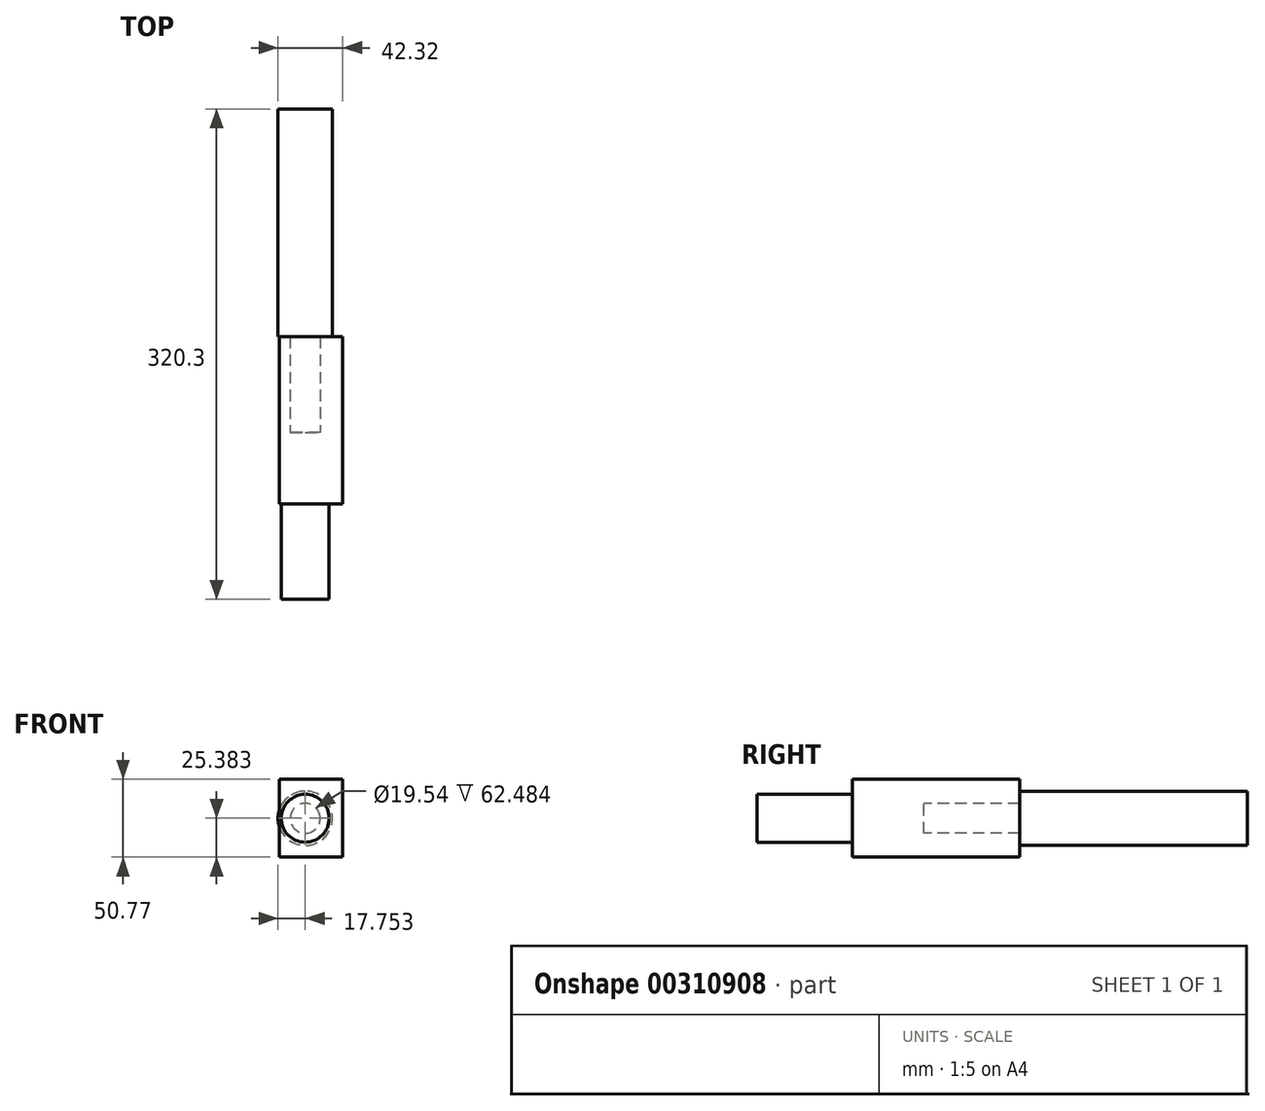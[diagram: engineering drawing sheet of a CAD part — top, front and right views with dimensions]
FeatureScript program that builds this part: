
annotation { "Feature Type Name" : "Feature", "Feature Type Description" : "" }
export const myFeature = defineFeature(function(context is Context, id is Id, definition is map)
    precondition{}
    {
        {
            var Q0;
            Q0=qCreatedBy(makeId("Front.planeOp"),FACE);
            var sketch = newSketch(context, id + "F0", { "sketchPlane" : qUnion([Q0])});
            skLineSegment(sketch, "E0.bottom", {"start": v(-108.3, 0) * mm, "end": v(-66.8, 0) * mm});
            skLineSegment(sketch, "E0.top", {"start": v(-108.3, -50.77) * mm, "end": v(-66.8, -50.77) * mm});
            skLineSegment(sketch, "E0.left", {"start": v(-108.3, 0) * mm, "end": v(-108.3, -50.77) * mm});
            skLineSegment(sketch, "E0.right", {"start": v(-66.8, 0) * mm, "end": v(-66.8, -50.77) * mm});
            skCircle(sketch, "E1", {"center": v(-91.38, -25.39) * mm, "radius": 9.77 * mm});
            skPoint(sketch, "E1.centerSnap0", {"position": v(-108.3, -25.39) * mm});
            skSolve(sketch);
        }
        {
            var Q0;
            Q0=qSketchRegion(id+"F0",true);
            extrude(context, id + "F1", {"entities" : qUnion([Q0]), "oppositeDirection" : true, "depth" : 62.48 * mm});
        }
        {
            var Q0;
            Q0=makeQuery(id+"F1.opExtrude","CAP_FACE",FACE,{"disambiguationData":[OSD([sQuery(id+"F0.wireOp",EDGE,"E0.bottom"),sQuery(id+"F0.wireOp",EDGE,"E0.top"),sQuery(id+"F0.wireOp",EDGE,"E0.left"),sQuery(id+"F0.wireOp",EDGE,"E0.right"),sQuery(id+"F0.wireOp",EDGE,"E1")])],"isStart":true});
            var sketch = newSketch(context, id + "F2", { "sketchPlane" : qUnion([Q0])});
            skCircle(sketch, "E2", {"center": v(-91.38, -25.39) * mm, "radius": 15.64 * mm});
            skSolve(sketch);
        }
        {
            var Q0;
            Q0=qSketchRegion(id+"F2",true);
            var Q1;
            Q1=makeQuery(id+"F1.opExtrude","CAP_FACE",FACE,{"disambiguationData":[OSD([sQuery(id+"F0.wireOp",EDGE,"E0.bottom"),sQuery(id+"F0.wireOp",EDGE,"E0.top"),sQuery(id+"F0.wireOp",EDGE,"E0.left"),sQuery(id+"F0.wireOp",EDGE,"E0.right"),sQuery(id+"F0.wireOp",EDGE,"E1")])],"isStart":false});
            extrude(context, id + "F3", {"entities" : qUnion([Q0, Q1]), "operationType" : NewBodyOperationType.ADD, "depth" : 108.97 * mm});
        }
        {
            var Q0;
            Q0=makeQuery(id+"F1.opExtrude","CAP_FACE",FACE,{"disambiguationData":[OSD([sQuery(id+"F0.wireOp",EDGE,"E0.bottom"),sQuery(id+"F0.wireOp",EDGE,"E0.top"),sQuery(id+"F0.wireOp",EDGE,"E0.left"),sQuery(id+"F0.wireOp",EDGE,"E0.right"),sQuery(id+"F0.wireOp",EDGE,"E1")])],"isStart":false});
            var sketch = newSketch(context, id + "F4", { "sketchPlane" : qUnion([Q0])});
            skCircle(sketch, "E3", {"center": v(91.38, -25.39) * mm, "radius": 17.75 * mm});
            skSolve(sketch);
        }
        {
            var Q0;
            Q0=qSketchRegion(id+"F4",true);
            extrude(context, id + "F5", {"entities" : qUnion([Q0]), "operationType" : NewBodyOperationType.ADD, "depth" : 148.84 * mm});
        }
    });
